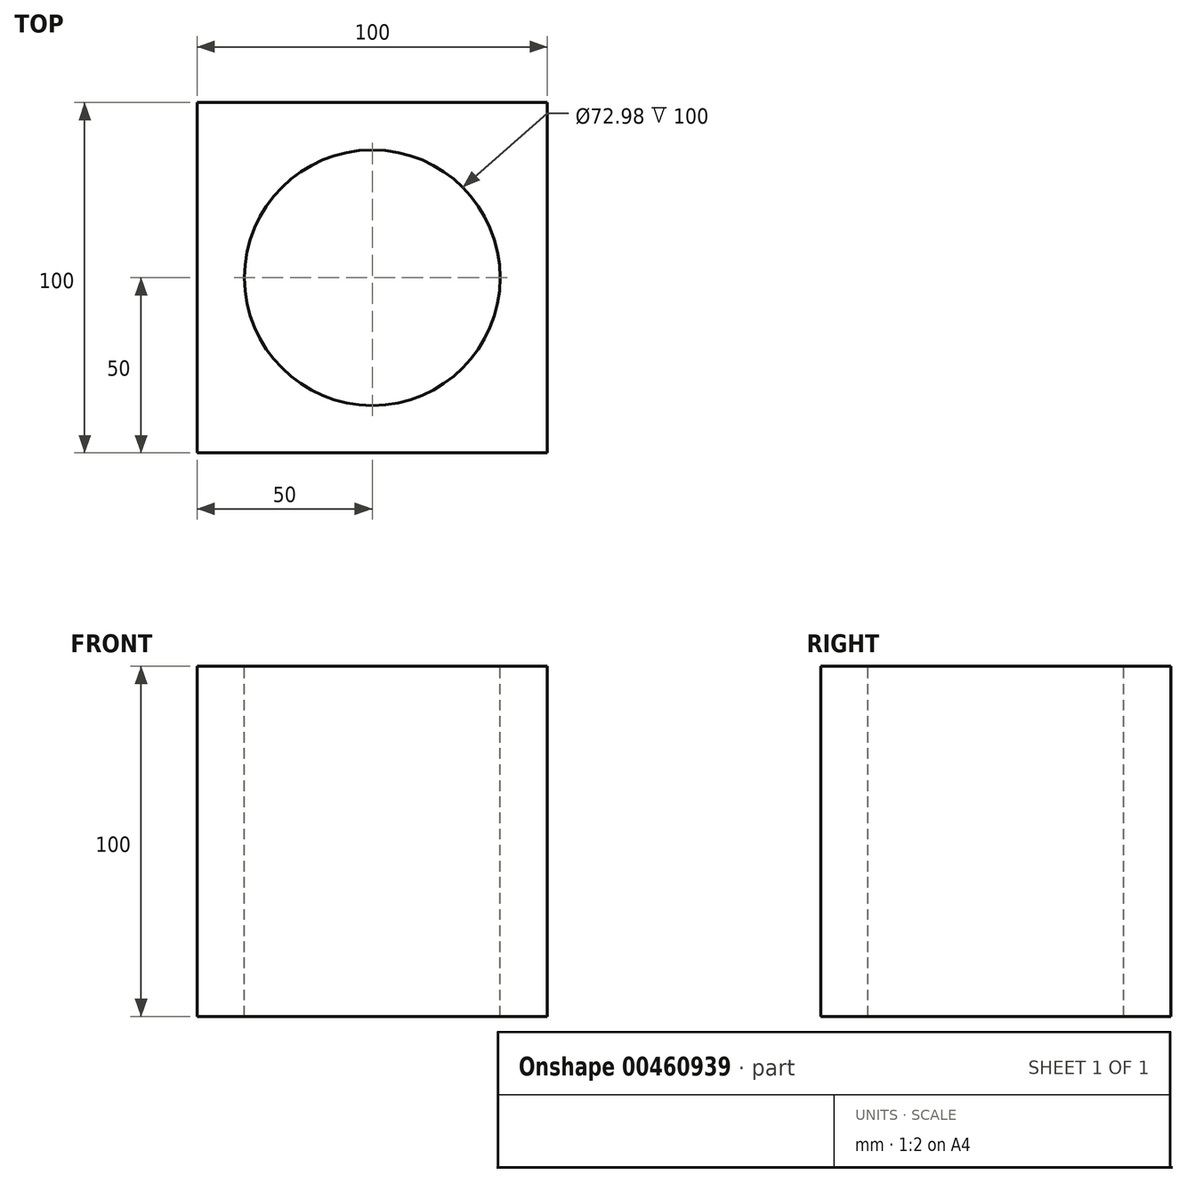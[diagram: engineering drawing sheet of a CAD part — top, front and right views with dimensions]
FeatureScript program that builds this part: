
annotation { "Feature Type Name" : "Feature", "Feature Type Description" : "" }
export const myFeature = defineFeature(function(context is Context, id is Id, definition is map)
    precondition{}
    {
        {
            var Q0;
            Q0=qCreatedBy(makeId("Front.planeOp"),FACE);
            var sketch = newSketch(context, id + "F0", { "sketchPlane" : qUnion([Q0])});
            skLineSegment(sketch, "E0.bottom", {"start": v(50, 50) * mm, "end": v(-50, 50) * mm});
            skLineSegment(sketch, "E0.top", {"start": v(50, -50) * mm, "end": v(-50, -50) * mm});
            skLineSegment(sketch, "E0.left", {"start": v(50, 50) * mm, "end": v(50, -50) * mm});
            skLineSegment(sketch, "E0.right", {"start": v(-50, 50) * mm, "end": v(-50, -50) * mm});
            skPoint(sketch, "E0.middle", {"position": v(0, 0) * mm});
            skSolve(sketch);
        }
        {
            var Q0;
            Q0=makeQuery(id+"F0.imprint","IMPRINT",FACE,{"disambiguationData":[TD([[makeQuery(id+"F0.imprint","IMPRINT",EDGE,{"derivedFrom":sQuery(id+"F0.wireOp",EDGE,"E0.bottom")}),1.0]])]});
            extrude(context, id + "F1", {"entities" : qUnion([Q0]), "depth" : 100 * mm, "symmetric" : true});
        }
        {
            var Q0;
            Q0=makeQuery(id+"F1.opExtrude","SWEPT_FACE",FACE,{"disambiguationData":[OSD([sQuery(id+"F0.wireOp",EDGE,"E0.bottom")])]});
            var sketch = newSketch(context, id + "F2", { "sketchPlane" : qUnion([Q0])});
            skCircle(sketch, "E1", {"center": v(0, 0) * mm, "radius": 36.5 * mm});
            skSolve(sketch);
        }
        {
            var Q0;
            Q0=makeQuery(id+"F2.imprint","IMPRINT",FACE,{"disambiguationData":[TD([[makeQuery(id+"F2.imprint","IMPRINT",EDGE,{"derivedFrom":sQuery(id+"F2.wireOp",EDGE,"E1")}),1.0]])]});
            extrude(context, id + "F3", {"entities" : qUnion([Q0]), "operationType" : NewBodyOperationType.REMOVE, "endBound" : BoundingType.THROUGH_ALL, "oppositeDirection" : true, "depth" : 25 * mm});
        }
    });
